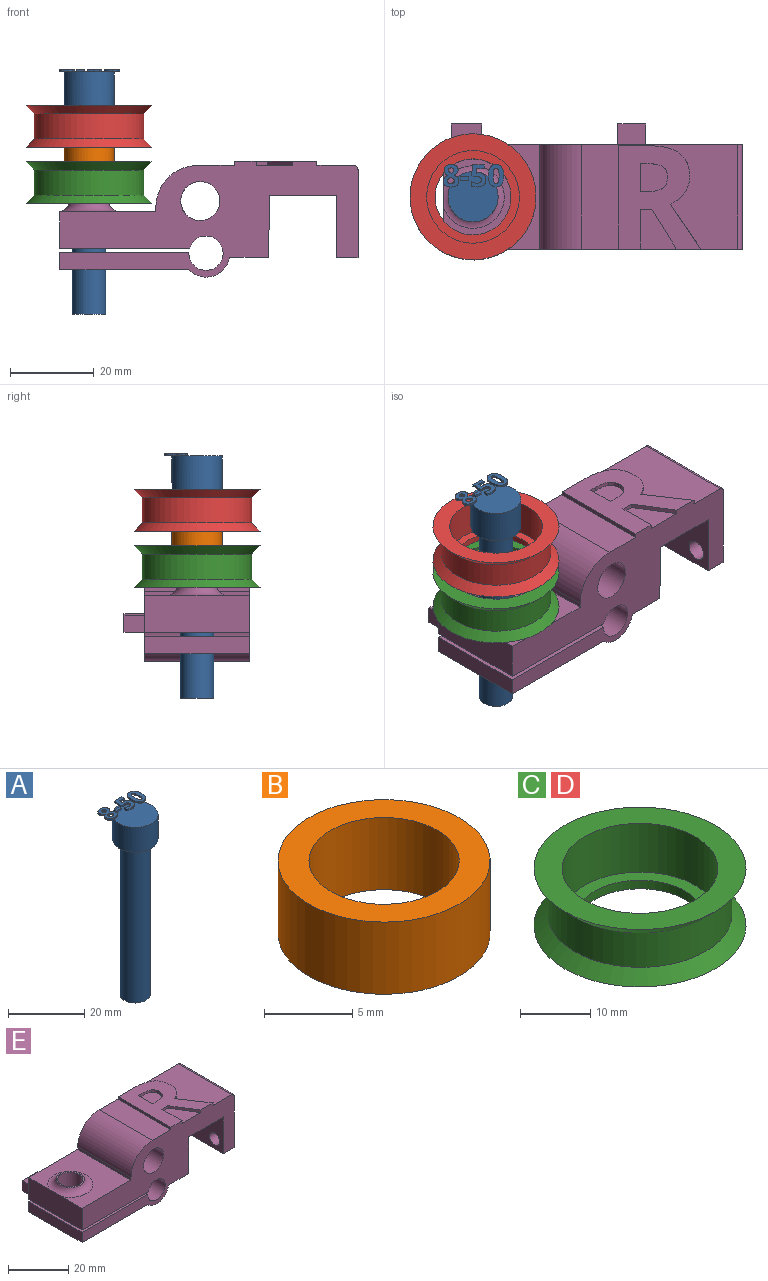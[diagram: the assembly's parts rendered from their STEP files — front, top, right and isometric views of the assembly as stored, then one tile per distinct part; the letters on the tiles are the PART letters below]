
ASSEMBLY  parts=5 mates=4
PART A: 86 faces, bbox 14.5x13.7x58.5 mm
  f0: plane 12x12mm, normal (0,0,1), area 99.4mm2, adj f5,f22,f23,f24,f25,f26,f40,f41
  f1: plane 1x0.26mm, normal (0,0,1), area 0.1mm2, adj f5,f46,f47,f48,f49
  f2: plane 0.85x0.68mm, normal (0,0,1), area 0.2mm2, adj f5,f29,f30,f31
  f3: cylinder r=4mm len=50mm, axis (0,0,-1), area 1256.6mm2, adj f4,f6
  f4: plane 8x8mm, normal (0,0,-1), area 50.3mm2, adj f3
  f5: cylinder r=6mm len=12mm, axis (0,0,-1), area 301.6mm2, adj f0,f1,f2,f6,f39,f45,f67,f85
  f6: plane 12x12mm, normal (0,0,-1), area 62.8mm2, adj f3,f5
  f7: extruded ~0.5x0.46mm, area 0.2mm2, adj f8,f37,f38,f39
  f8: extruded ~0.5x0.46mm, area 0.2mm2, adj f7,f9,f38,f39
  f9: extruded ~0.5x0.39mm, area 0.2mm2, adj f8,f10,f38,f39
  f10: extruded ~0.5x0.4mm, area 0.2mm2, adj f9,f11,f38,f39
  f11: extruded ~0.5x0.49mm, area 0.3mm2, adj f10,f12,f38,f39
  f12: extruded ~0.5x0.5mm, area 0.3mm2, adj f11,f13,f38,f39
  f13: extruded ~0.5x0.39mm, area 0.2mm2, adj f12,f37,f38,f39
  f14: extruded ~1.22x0.5mm, area 0.6mm2, adj f15,f35,f38,f39
  f15: extruded ~1.22x0.5mm, area 0.6mm2, adj f14,f16,f38,f39
  f16: extruded ~0.91x0.5mm, area 0.5mm2, adj f15,f17,f38,f39
  f17: extruded ~0.71x0.5mm, area 0.4mm2, adj f16,f18,f38,f39
  f18: extruded ~0.65x0.61mm, area 0.4mm2, adj f17,f19,f38,f39
  f19: extruded ~0.77x0.62mm, area 0.5mm2, adj f18,f20,f38,f39
  f20: extruded ~0.8x0.5mm, area 0.4mm2, adj f19,f21,f38,f39
  f21: extruded ~1.04x0.5mm, area 0.6mm2, adj f20,f22,f38,f39
  f22: extruded ~1.36x0.5mm, area 0.7mm2, adj f0,f21,f23,f38,f39
  f23: extruded ~1.33x0.5mm, area 0.7mm2, adj f0,f22,f24,f38
  f24: extruded ~1.04x0.51mm, area 0.6mm2, adj f0,f23,f25,f38
  f25: extruded ~0.75x0.5mm, area 0.4mm2, adj f0,f24,f26,f38
  f26: extruded ~0.85x0.66mm, area 0.5mm2, adj f0,f25,f27,f38,f39
  f27: extruded ~0.72x0.56mm, area 0.5mm2, adj f26,f28,f38,f39
  f28: extruded ~0.72x0.5mm, area 0.4mm2, adj f27,f35,f38,f39
  f29: extruded ~0.5x0.45mm, area 0.3mm2, adj f2,f30,f36,f38,f39
  f30: extruded ~0.5x0.47mm, area 0.3mm2, adj f2,f29,f31,f38
  f31: extruded ~0.62x0.5mm, area 0.3mm2, adj f2,f30,f32,f38,f39
  f32: extruded ~0.59x0.5mm, area 0.3mm2, adj f31,f33,f38,f39
  f33: extruded ~0.5x0.48mm, area 0.3mm2, adj f32,f34,f38,f39
  f34: extruded ~0.89x0.77mm, area 0.6mm2, adj f33,f36,f38,f39
  f35: extruded ~0.93x0.5mm, area 0.5mm2, adj f14,f28,f38,f39
  f36: extruded ~0.66x0.5mm, area 0.4mm2, adj f29,f34,f38,f39
  f37: extruded ~0.5x0.39mm, area 0.2mm2, adj f7,f13,f38,f39
  f38: plane 5.4x3.69mm, normal (0,0,1), area 12.7mm2, adj f7,f8,f9,f10,f11,f12,f13,f14
  f39: plane 5.4x3.53mm, normal (0,0,-1), area 10.2mm2, adj f5,f7,f8,f9,f10,f11,f12,f13
  f40: plane 0.9x0.5mm, normal (-1,0,0), area 0.4mm2, adj f0,f41,f43,f44
  f41: plane 1.93x0.5mm, normal (0,-1,0), area 1mm2, adj f0,f40,f42,f44
  f42: plane 0.9x0.5mm, normal (1,0,0), area 0.4mm2, adj f0,f41,f43,f44
  f43: plane 1.93x0.5mm, normal (0,1,0), area 1mm2, adj f0,f40,f42,f44
  f44: plane 1.93x0.9mm, normal (0,0,1), area 1.7mm2, adj f40,f41,f42,f43
  f45: plane 0.76x0.31mm, normal (0,0,-1), area 0mm2, adj f5,f46
  f46: extruded ~1.21x0.5mm, area 0.7mm2, adj f0,f1,f45,f47,f65,f66
  f47: extruded ~0.54x0.5mm, area 0.3mm2, adj f1,f46,f48,f66
  f48: plane 0.5x0.13mm, normal (-0.2,0.98,0), area 0.1mm2, adj f1,f47,f49,f66
  f49: plane 1.03x0.5mm, normal (1,-0.09,0), area 0.5mm2, adj f1,f48,f50,f66,f67
  f50: plane 1.88x0.5mm, normal (0,-1,0), area 0.9mm2, adj f49,f51,f66,f67
  f51: plane 0.94x0.5mm, normal (1,0,0), area 0.5mm2, adj f50,f52,f66,f67
  f52: plane 2.85x0.5mm, normal (0,1,0), area 1.4mm2, adj f51,f53,f66,f67
  f53: plane 2.68x0.5mm, normal (-1,0.07,0), area 1.3mm2, adj f0,f52,f54,f66,f67
  f54: plane 0.5x0.44mm, normal (-0.47,-0.88,0), area 0.3mm2, adj f0,f53,f55,f66
  f55: extruded ~0.5x0.37mm, area 0.2mm2, adj f0,f54,f56,f66
  f56: extruded ~0.5x0.42mm, area 0.2mm2, adj f0,f55,f57,f66
  f57: extruded ~1.05x0.8mm, area 0.8mm2, adj f0,f56,f58,f66
  f58: extruded ~1.02x0.83mm, area 0.8mm2, adj f0,f57,f59,f66
  f59: extruded ~0.72x0.5mm, area 0.4mm2, adj f0,f58,f60,f66
  f60: extruded ~0.66x0.5mm, area 0.4mm2, adj f0,f59,f61,f66
  f61: plane 0.96x0.5mm, normal (-1,0,0), area 0.5mm2, adj f0,f60,f62,f66
  f62: extruded ~1.42x0.5mm, area 0.7mm2, adj f0,f61,f63,f66
  f63: extruded ~1.55x0.5mm, area 0.8mm2, adj f0,f62,f64,f66
  f64: extruded ~1.36x0.54mm, area 0.8mm2, adj f0,f63,f65,f66
  f65: extruded ~1.17x0.5mm, area 0.6mm2, adj f0,f46,f64,f66
  f66: plane 5.33x3.51mm, normal (0,0,1), area 10.9mm2, adj f46,f47,f48,f49,f50,f51,f52,f53
  f67: plane 2.97x1.71mm, normal (0,0,-1), area 3.5mm2, adj f5,f49,f50,f51,f52,f53
  f68: extruded ~1.39x0.5mm, area 0.7mm2, adj f69,f83,f84,f85
  f69: extruded ~1.39x0.5mm, area 0.7mm2, adj f68,f70,f84,f85
  f70: extruded ~0.56x0.5mm, area 0.4mm2, adj f69,f71,f84,f85
  f71: extruded ~0.56x0.5mm, area 0.4mm2, adj f70,f72,f84,f85
  f72: extruded ~1.39x0.5mm, area 0.7mm2, adj f71,f73,f84,f85
  f73: extruded ~1.38x0.5mm, area 0.7mm2, adj f72,f74,f84,f85
  f74: extruded ~0.56x0.5mm, area 0.4mm2, adj f73,f83,f84,f85
  f75: extruded ~2.04x0.5mm, area 1.1mm2, adj f76,f82,f84,f85
  f76: extruded ~2.02x0.5mm, area 1.1mm2, adj f75,f77,f84,f85
  f77: extruded ~1.38x0.69mm, area 0.8mm2, adj f76,f78,f84,f85
  f78: extruded ~1.38x0.66mm, area 0.8mm2, adj f77,f79,f84,f85
  f79: extruded ~2.05x0.5mm, area 1.1mm2, adj f78,f80,f84,f85
  f80: extruded ~2.02x0.5mm, area 1mm2, adj f0,f79,f81,f84,f85
  f81: extruded ~1.37x0.68mm, area 0.8mm2, adj f0,f80,f82,f84
  f82: extruded ~1.39x0.66mm, area 0.8mm2, adj f0,f75,f81,f84,f85
  f83: extruded ~0.56x0.5mm, area 0.4mm2, adj f68,f74,f84,f85
  f84: plane 5.41x3.68mm, normal (0,0,1), area 12.1mm2, adj f68,f69,f70,f71,f72,f73,f74,f75
  f85: plane 5.41x3.68mm, normal (0,0,-1), area 10.3mm2, adj f5,f68,f69,f70,f71,f72,f73,f74
PART B: 4 faces, bbox 12x12x5 mm
  f0: cylinder r=4.25mm len=8.5mm, axis (0,0,-1), area 133.5mm2, adj f2,f3
  f1: cylinder r=6mm len=12mm, axis (0,0,-1), area 188.5mm2, adj f2,f3
  f2: plane 12x12mm, normal (0,0,1), area 56.4mm2, adj f0,f1
  f3: plane 12x12mm, normal (0,0,-1), area 56.4mm2, adj f0,f1
PART C: 8 faces, bbox 30.2x30.2x10 mm
  f0: plane 30.2x30.2mm, normal (0,0,1), area 329.2mm2, adj f1,f7
  f1: cylinder r=11.1mm len=22.2mm, axis (0,0,-1), area 592.8mm2, adj f0,f2
  f2: plane 22.2x22.2mm, normal (0,0,1), area 126.9mm2, adj f1,f3
  f3: cylinder r=9.1mm len=18.2mm, axis (0,0,-1), area 85.8mm2, adj f2,f4
  f4: plane 30.2x30.2mm, normal (0,0,-1), area 456.2mm2, adj f3,f5
  f5: cone r=13.1mm half-angle=45deg, axis (0,0,-1), area 250.6mm2, adj f4,f6
  f6: cylinder r=13.1mm len=26.2mm, axis (0,0,-1), area 493.9mm2, adj f5,f7
  f7: cone r=15.1mm half-angle=45deg, axis (0,0,1), area 250.6mm2, adj f0,f6
PART D: same geometry as C
PART E: 56 faces, bbox 74.9x30x27.7 mm
  f0: plane 37.42x25mm, normal (0,0,1), area 542.1mm2, adj f14,f15,f25,f27,f40,f41,f42,f43
  f1: plane 9.51x8.71mm, normal (0,0,1), area 54.7mm2, adj f14,f37,f38,f39
  f2: plane 25x4.12mm, normal (-1,0,0), area 103mm2, adj f5,f14,f15,f19
  f3: cylinder r=4.17mm len=8.35mm, axis (0,0,1), area 108.1mm2, adj f5,f19
  f4: plane 25x9.34mm, normal (0,0,-1), area 233.4mm2, adj f13,f14,f15,f17
  f5: plane 30.88x25mm, normal (0,0,-1), area 717.2mm2, adj f2,f3,f14,f15,f17
  f6: plane 25x8.82mm, normal (-1,0,0), area 219.6mm2, adj f7,f14,f15,f20,f24
  f7: plane 25x23mm, normal (0,0,1), area 400mm2, adj f6,f8,f14,f15,f24
  f8: plane 25x1.1mm, normal (-1,0,0), area 27.5mm2, adj f7,f14,f15,f25
  f9: plane 25x21.09mm, normal (1,0,0), area 493.5mm2, adj f10,f14,f15,f22,f23,f27
  f10: plane 25x5.05mm, normal (0,0,-1), area 126.2mm2, adj f9,f11,f14,f15
  f11: plane 25x15mm, normal (-1,0,0), area 341.3mm2, adj f10,f12,f14,f15,f22,f23
  f12: plane 25x16.15mm, normal (0,0,-1), area 403.8mm2, adj f11,f13,f14,f15
  f13: plane 25x14.91mm, normal (1,0,-0.01), area 372.8mm2, adj f4,f12,f14,f15
  f14: plane 71.42x27.75mm, normal (0,-1,0), area 1041.1mm2, adj f0,f1,f2,f4,f5,f6,f7,f8
  f15: plane 71.42x26.75mm, normal (0,1,0), area 970.1mm2, adj f0,f2,f4,f5,f6,f7,f8,f9
  f16: cylinder r=4.17mm len=10.78mm, axis (0,0,1), area 282.8mm2, adj f20,f21
  f17: cylinder r=5.75mm len=25mm, axis (0,-1,0), area 315.9mm2, adj f4,f5,f14,f15
  f18: cylinder r=4.1mm len=25mm, axis (0,-1,0), area 618.7mm2, adj f14,f15,f19,f20
  f19: plane 30.91x25mm, normal (0,0,1), area 718.1mm2, adj f2,f3,f14,f15,f18
  f20: plane 31.07x30mm, normal (0,0,-1), area 758.4mm2, adj f6,f14,f15,f16,f18,f29,f30,f31
  f21: plane 9.35x9.35mm, normal (0,0,1), area 13.9mm2, adj f16,f24
  f22: cylinder r=2.43mm len=5.05mm, axis (1,0,0), area 77mm2, adj f9,f11
  f23: cylinder r=2.2mm len=5.05mm, axis (1,0,0), area 69.8mm2, adj f9,f11
  f24: torus R=7.5mm, axis (0,0,-1), area 134.6mm2, adj f6,f7,f21
  f25: cylinder r=10mm len=25mm, axis (0,-1,0), area 392.7mm2, adj f0,f8,f14,f15
  f26: cylinder r=4.68mm len=25mm, axis (0,-1,0), area 735.2mm2, adj f14,f15
  f27: cylinder r=1mm len=25mm, axis (0,-1,0), area 39.3mm2, adj f0,f9,f14,f15
  f28: plane 7.3x5mm, normal (0,0,1), area 36.5mm2, adj f15,f29,f30,f31
  f29: plane 5x4.12mm, normal (-1,0,0), area 20.6mm2, adj f15,f20,f28,f31
  f30: plane 5x4.12mm, normal (1,0,0), area 20.6mm2, adj f15,f20,f28,f31
  f31: plane 7.3x4.12mm, normal (0,1,0), area 30.1mm2, adj f20,f28,f29,f30
  f32: plane 6.63x5mm, normal (0,0,1), area 33.2mm2, adj f15,f33,f35,f36
  f33: plane 5x4.5mm, normal (-1,0,0), area 22.5mm2, adj f15,f32,f34,f36
  f34: plane 6.63x5mm, normal (0,0,-1), area 33.2mm2, adj f15,f33,f35,f36
  f35: plane 5x4.5mm, normal (1,0,0), area 22.5mm2, adj f15,f32,f34,f36
  f36: plane 6.63x4.5mm, normal (0,1,0), area 29.9mm2, adj f32,f33,f34,f35
  f37: plane 9.51x1mm, normal (1,0,0), area 9.5mm2, adj f1,f14,f38,f54
  f38: plane 2.79x1mm, normal (0,-1,0), area 2.8mm2, adj f1,f37,f39,f54
  f39: plane 9.51x5.92mm, normal (-0.85,-0.53,0), area 11.2mm2, adj f1,f14,f38,f54
  f40: extruded ~10.8x7.29mm, area 13mm2, adj f0,f14,f41,f54
  f41: extruded ~3.41x2.67mm, area 4.4mm2, adj f0,f40,f42,f54
  f42: extruded ~3.89x1.2mm, area 4.1mm2, adj f0,f41,f43,f54
  f43: extruded ~5.59x2.42mm, area 6.3mm2, adj f0,f42,f44,f54
  f44: extruded ~7.48x1.84mm, area 7.8mm2, adj f0,f43,f45,f54
  f45: plane 7.22x1mm, normal (0,1,0), area 7.2mm2, adj f0,f44,f46,f54
  f46: plane 24.79x1mm, normal (-1,0,0), area 24.8mm2, adj f0,f14,f45,f54
  f47: plane 1.69x1mm, normal (0,1,0), area 1.7mm2, adj f48,f53,f54,f55
  f48: plane 6.7x1mm, normal (1,0,0), area 6.7mm2, adj f47,f49,f54,f55
  f49: plane 1.6x1mm, normal (0,-1,0), area 1.6mm2, adj f48,f50,f54,f55
  f50: extruded ~3.75x1mm, area 3.9mm2, adj f49,f51,f54,f55
  f51: extruded ~2.51x1.21mm, area 2.9mm2, adj f50,f52,f54,f55
  f52: extruded ~2.61x1.19mm, area 3mm2, adj f51,f53,f54,f55
  f53: extruded ~3.68x1mm, area 3.8mm2, adj f47,f52,f54,f55
  f54: plane 24.79x19.8mm, normal (0,0,1), area 300mm2, adj f14,f37,f38,f39,f40,f41,f42,f43
  f55: plane 6.7x6.56mm, normal (0,0,1), area 38.8mm2, adj f47,f48,f49,f50,f51,f52,f53
PLACE A t=(-103.78,-12.5,-13.6)mm
PLACE B rot(axis=(1,0,0),180deg) t=(-103.78,-12.5,26.4)mm
PLACE C t=(-103.78,-12.5,18.1)mm
PLACE D t=(-103.78,-12.5,31.6)mm
PLACE E at identity
MATE fastened A.f3 <-> D.f1  axis (0,0,-1) through (-103.78,-12.5,36.4)mm
MATE fastened B.f0 <-> C.f1  axis (0,0,1) through (-103.78,-12.5,21.4)mm
MATE fastened C.f1 <-> E.f3  axis (0,0,-1) through (-103.78,-12.5,12.9)mm
MATE fastened D.f1 <-> B.f0  axis (0,0,-1) through (-103.78,-12.5,26.4)mm
